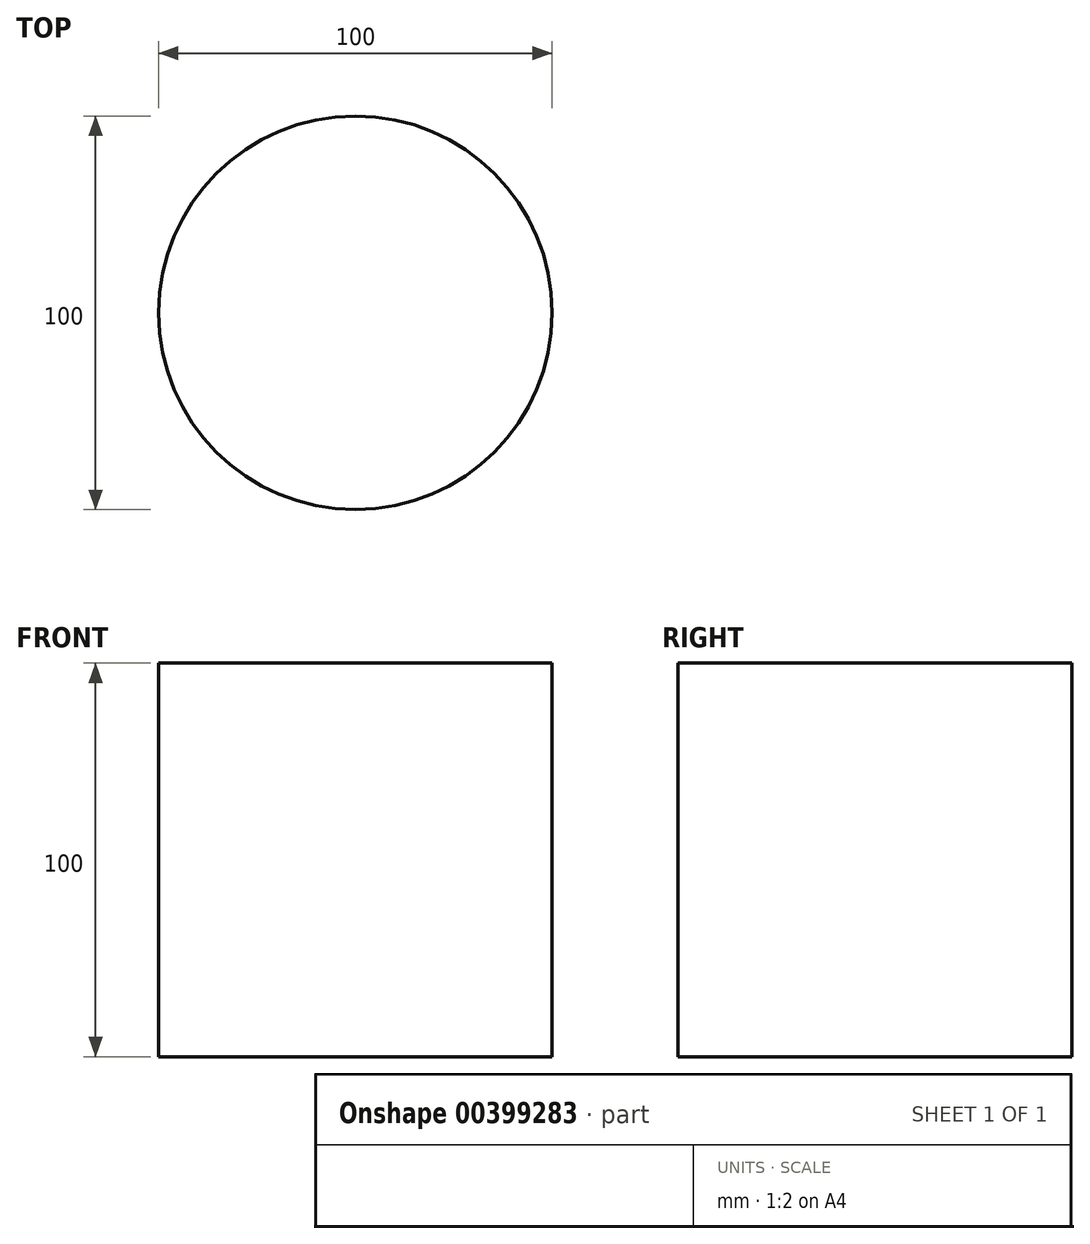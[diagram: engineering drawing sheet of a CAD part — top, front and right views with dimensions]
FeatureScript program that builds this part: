
annotation { "Feature Type Name" : "Feature", "Feature Type Description" : "" }
export const myFeature = defineFeature(function(context is Context, id is Id, definition is map)
    precondition{}
    {
        {
            var Q0;
            Q0=qCreatedBy(makeId("Top.planeOp"),FACE);
            var sketch = newSketch(context, id + "F0", { "sketchPlane" : qUnion([Q0])});
            skCircle(sketch, "E0", {"center": v(0, 0) * mm, "radius": 50 * mm});
            skSolve(sketch);
        }
        {
            var Q0;
            Q0 = qSketchRegion(id + "F0", true);
            extrude(context, id + "F1", {"entities" : qUnion([Q0]), "depth" : 100 * mm});
        }
    });
